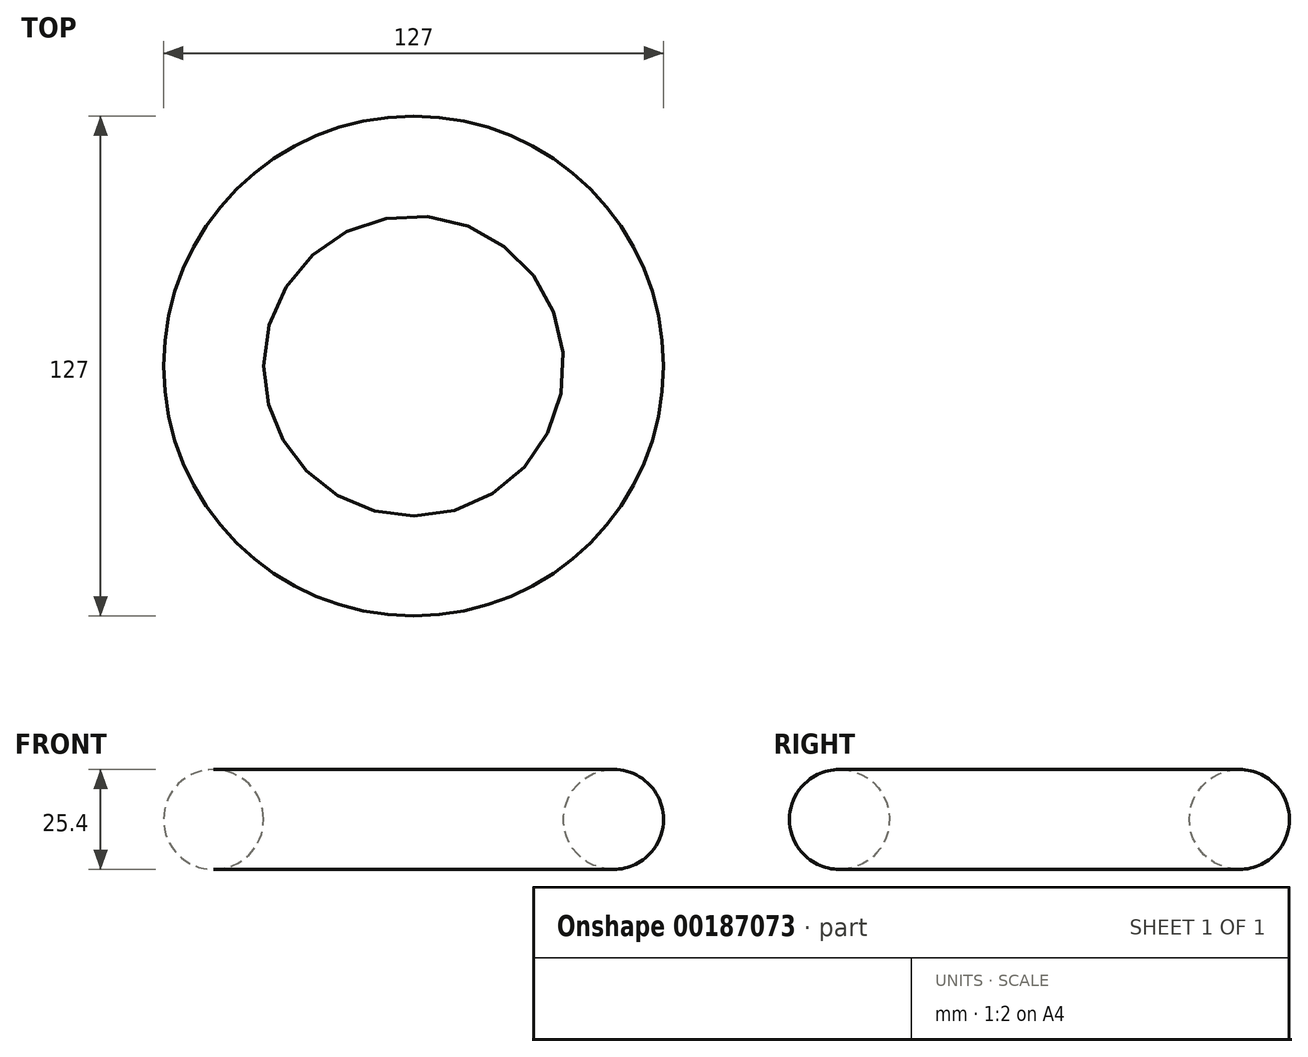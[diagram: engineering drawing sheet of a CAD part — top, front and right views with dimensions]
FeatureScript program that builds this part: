
annotation { "Feature Type Name" : "Feature", "Feature Type Description" : "" }
export const myFeature = defineFeature(function(context is Context, id is Id, definition is map)
    precondition{}
    {
        {
            var Q0;
            Q0=qCreatedBy(makeId("Front.planeOp"),FACE);
            var sketch = newSketch(context, id + "F0", { "sketchPlane" : qUnion([Q0])});
            skCircle(sketch, "E0", {"center": v(50.8, 0) * mm, "radius": 12.7 * mm});
            skLineSegment(sketch, "E1", {"start": v(0, 0) * mm, "end": v(0, 23.33) * mm});
            skSolve(sketch);
        }
        {
            var Q0;
            Q0=makeQuery(id+"F0.imprint","IMPRINT",FACE,{"disambiguationData":[TD([[makeQuery(id+"F0.imprint","IMPRINT",EDGE,{"derivedFrom":sQuery(id+"F0.wireOp",EDGE,"E0")}),1.0]])]});
            var Q1;
            Q1=sQuery(id+"F0.wireOp",EDGE,"E1");
            revolve(context, id + "F1", {"entities" : qUnion([Q0]), "axis" : qUnion([Q1]), "revolveType" : RevolveType.FULL});
        }
    });
